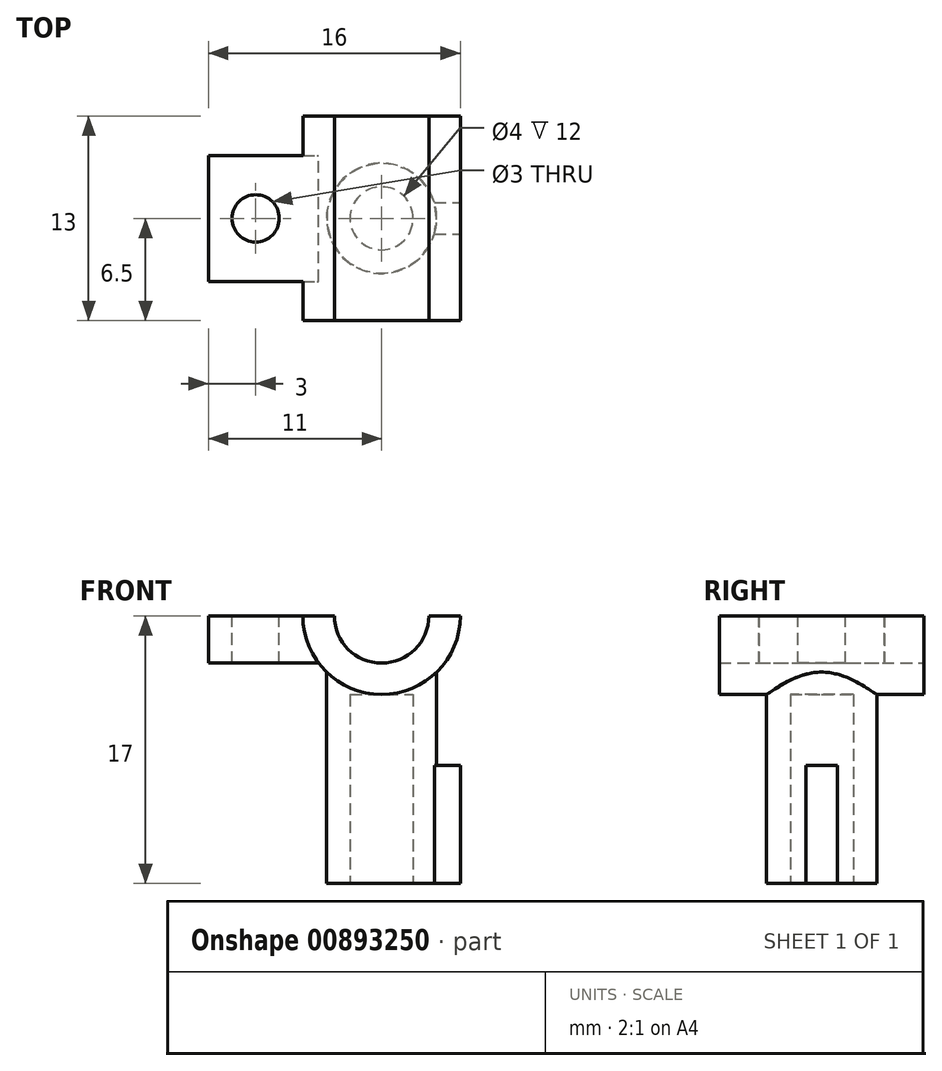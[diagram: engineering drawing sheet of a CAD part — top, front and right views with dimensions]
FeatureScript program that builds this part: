
annotation { "Feature Type Name" : "Feature", "Feature Type Description" : "" }
export const myFeature = defineFeature(function(context is Context, id is Id, definition is map)
    precondition{}
    {
        {
            var Q0;
            Q0=qCreatedBy(makeId("Front.planeOp"),FACE);
            var sketch = newSketch(context, id + "F0", { "sketchPlane" : qUnion([Q0])});
            skArc(sketch, "E0", {"start": v(-5, 0) * mm, "mid": v(0, -5) * mm, "end": v(5, 0) * mm});
            skArc(sketch, "E1", {"start": v(-3, 0) * mm, "mid": v(0, -3) * mm, "end": v(3, 0) * mm});
            skLineSegment(sketch, "E2", {"start": v(-5, 0) * mm, "end": v(-3, 0) * mm});
            skLineSegment(sketch, "E3", {"start": v(3, 0) * mm, "end": v(5, 0) * mm});
            skSolve(sketch);
        }
        {
            var Q0;
            Q0 = qSketchRegion(id + "F0", true);
            extrude(context, id + "F1", {"entities" : qUnion([Q0]), "endBound" : BoundingType.SYMMETRIC, "depth" : 13 * mm, "offsetDistance" : 25 * mm});
        }
        {
            var Q0;
            Q0=qCreatedBy(makeId("Top.planeOp"),FACE);
            var sketch = newSketch(context, id + "F2", { "sketchPlane" : qUnion([Q0])});
            skLineSegment(sketch, "E4.bottom", {"start": v(-11, 4) * mm, "end": v(-3, 4) * mm});
            skLineSegment(sketch, "E4.top", {"start": v(-11, -4) * mm, "end": v(-3, -4) * mm});
            skLineSegment(sketch, "E4.left", {"start": v(-11, 4) * mm, "end": v(-11, -4) * mm});
            skLineSegment(sketch, "E4.right", {"start": v(-3, 4) * mm, "end": v(-3, -4) * mm});
            skSolve(sketch);
        }
        {
            var Q0;
            Q0 = qSketchRegion(id + "F2", true);
            extrude(context, id + "F3", {"entities" : qUnion([Q0]), "operationType" : NewBodyOperationType.ADD, "oppositeDirection" : true, "depth" : 3 * mm, "offsetDistance" : 25 * mm});
        }
        {
            var Q0;
            Q0=qCreatedBy(makeId("Top.planeOp"),FACE);
            var sketch = newSketch(context, id + "F4", { "sketchPlane" : qUnion([Q0])});
            skCircle(sketch, "E5", {"center": v(0, 0) * mm, "radius": 3.5 * mm});
            skSolve(sketch);
        }
        {
            var Q0;
            Q0 = qSketchRegion(id + "F4", true);
            extrude(context, id + "F5", {"entities" : qUnion([Q0]), "operationType" : NewBodyOperationType.ADD, "oppositeDirection" : true, "depth" : 17 * mm, "offsetDistance" : 25 * mm});
        }
        {
            var Q0;
            Q0=qCreatedBy(makeId("Front.planeOp"),FACE);
            var sketch = newSketch(context, id + "F6", { "sketchPlane" : qUnion([Q0])});
            skCircle(sketch, "E6", {"center": v(0, 0) * mm, "radius": 3 * mm});
            skSolve(sketch);
        }
        {
            var Q0;
            Q0 = qSketchRegion(id + "F6", true);
            extrude(context, id + "F7", {"entities" : qUnion([Q0]), "operationType" : NewBodyOperationType.REMOVE, "endBound" : BoundingType.SYMMETRIC, "depth" : 18.6 * mm, "offsetDistance" : 25 * mm});
        }
        {
            var Q0;
            Q0=makeQuery(id+"F5.opExtrude","CAP_FACE",FACE,{"disambiguationData":[OSD([sQuery(id+"F4.wireOp",EDGE,"E5")])],"isStart":false});
            var sketch = newSketch(context, id + "F8", { "sketchPlane" : qUnion([Q0])});
            skCircle(sketch, "E7", {"center": v(0, 0) * mm, "radius": 2 * mm});
            skSolve(sketch);
        }
        {
            var Q0;
            Q0 = qSketchRegion(id + "F8", true);
            extrude(context, id + "F9", {"entities" : qUnion([Q0]), "operationType" : NewBodyOperationType.REMOVE, "oppositeDirection" : true, "depth" : 12 * mm, "offsetDistance" : 25 * mm});
        }
        {
            var Q0;
            {var subQ0=sQuery(id+"F0.wireOp",EDGE,"E1");var subQ1=sQuery(id+"F0.wireOp",EDGE,"E3");var subQ2=sQuery(id+"F0.wireOp",EDGE,"E2");var subQ3=sQuery(id+"F0.wireOp",EDGE,"E0");var subQ4=sQuery(id+"F2.wireOp",EDGE,"E4.bottom");var subQ5=sQuery(id+"F2.wireOp",EDGE,"E4.top");var subQ6=sQuery(id+"F2.wireOp",EDGE,"E4.left");Q0=makeQuery(id+"F7.boolean.opBoolean","SPLIT",FACE,{"disambiguationData":[TD([makeQuery(id+"F1.opExtrude","SWEPT_FACE",FACE,{"disambiguationData":[OSD([subQ3])]}),makeQuery(id+"F1.opExtrude","CAP_FACE",FACE,{"disambiguationData":[OSD([subQ3,subQ0,subQ2,subQ1])],"isStart":true}),makeQuery(id+"F1.opExtrude","CAP_FACE",FACE,{"disambiguationData":[OSD([subQ3,subQ0,subQ2,subQ1])],"isStart":false}),makeQuery(id+"F1.opExtrude","SWEPT_FACE",FACE,{"disambiguationData":[OSD([subQ0])]}),makeQuery(id+"F3.opExtrude","SWEPT_FACE",FACE,{"disambiguationData":[OSD([subQ4])]}),makeQuery(id+"F3.opExtrude","SWEPT_FACE",FACE,{"disambiguationData":[OSD([subQ5])]}),makeQuery(id+"F3.opExtrude","SWEPT_FACE",FACE,{"disambiguationData":[OSD([subQ6])]}),makeQuery(id+"F7.opExtrude","SWEPT_FACE",FACE,{"disambiguationData":[OSD([sQuery(id+"F6.wireOp",EDGE,"E6")])]})])],"derivedFrom":makeQuery(id+"F5.boolean.opBoolean","MERGE",FACE,{"derivedFrom":[makeQuery(id+"F1.opExtrude","SWEPT_FACE",FACE,{"disambiguationData":[OSD([subQ1])]}),makeQuery(id+"F3.boolean.opBoolean","MERGE",FACE,{"derivedFrom":[makeQuery(id+"F1.opExtrude","SWEPT_FACE",FACE,{"disambiguationData":[OSD([subQ2])]}),makeQuery(id+"F3.opExtrude","CAP_FACE",FACE,{"disambiguationData":[OSD([subQ4,subQ5,subQ6,sQuery(id+"F2.wireOp",EDGE,"E4.right")])],"isStart":true})]}),makeQuery(id+"F5.opExtrude","CAP_FACE",FACE,{"disambiguationData":[OSD([sQuery(id+"F4.wireOp",EDGE,"E5")])],"isStart":true})]})});}
            var sketch = newSketch(context, id + "F10", { "sketchPlane" : qUnion([Q0])});
            skCircle(sketch, "E8", {"center": v(-8, 0) * mm, "radius": 1.5 * mm});
            skSolve(sketch);
        }
        {
            var Q0;
            Q0 = qSketchRegion(id + "F10", true);
            extrude(context, id + "F11", {"entities" : qUnion([Q0]), "operationType" : NewBodyOperationType.REMOVE, "endBound" : BoundingType.THROUGH_ALL, "oppositeDirection" : true, "depth" : 5 * mm, "offsetDistance" : 25 * mm});
        }
        {
            var Q0;
            Q0=makeQuery(id+"F5.opExtrude","CAP_FACE",FACE,{"disambiguationData":[OSD([sQuery(id+"F4.wireOp",EDGE,"E5")])],"isStart":false});
            var sketch = newSketch(context, id + "F12", { "sketchPlane" : qUnion([Q0])});
            skArc(sketch, "E9", {"start": v(3.35, -1) * mm, "mid": v(3.5, 0) * mm, "end": v(3.35, 1) * mm});
            skLineSegment(sketch, "E10", {"start": v(3.35, 1) * mm, "end": v(5, 1) * mm});
            skLineSegment(sketch, "E11", {"start": v(3.35, -1) * mm, "end": v(5, -1) * mm});
            skLineSegment(sketch, "E12", {"start": v(5, 1) * mm, "end": v(5, -1) * mm});
            skSolve(sketch);
        }
        {
            var Q0;
            Q0 = qSketchRegion(id + "F12", true);
            extrude(context, id + "F13", {"entities" : qUnion([Q0]), "operationType" : NewBodyOperationType.ADD, "oppositeDirection" : true, "depth" : 7.5 * mm, "offsetDistance" : 25 * mm});
        }
    });
